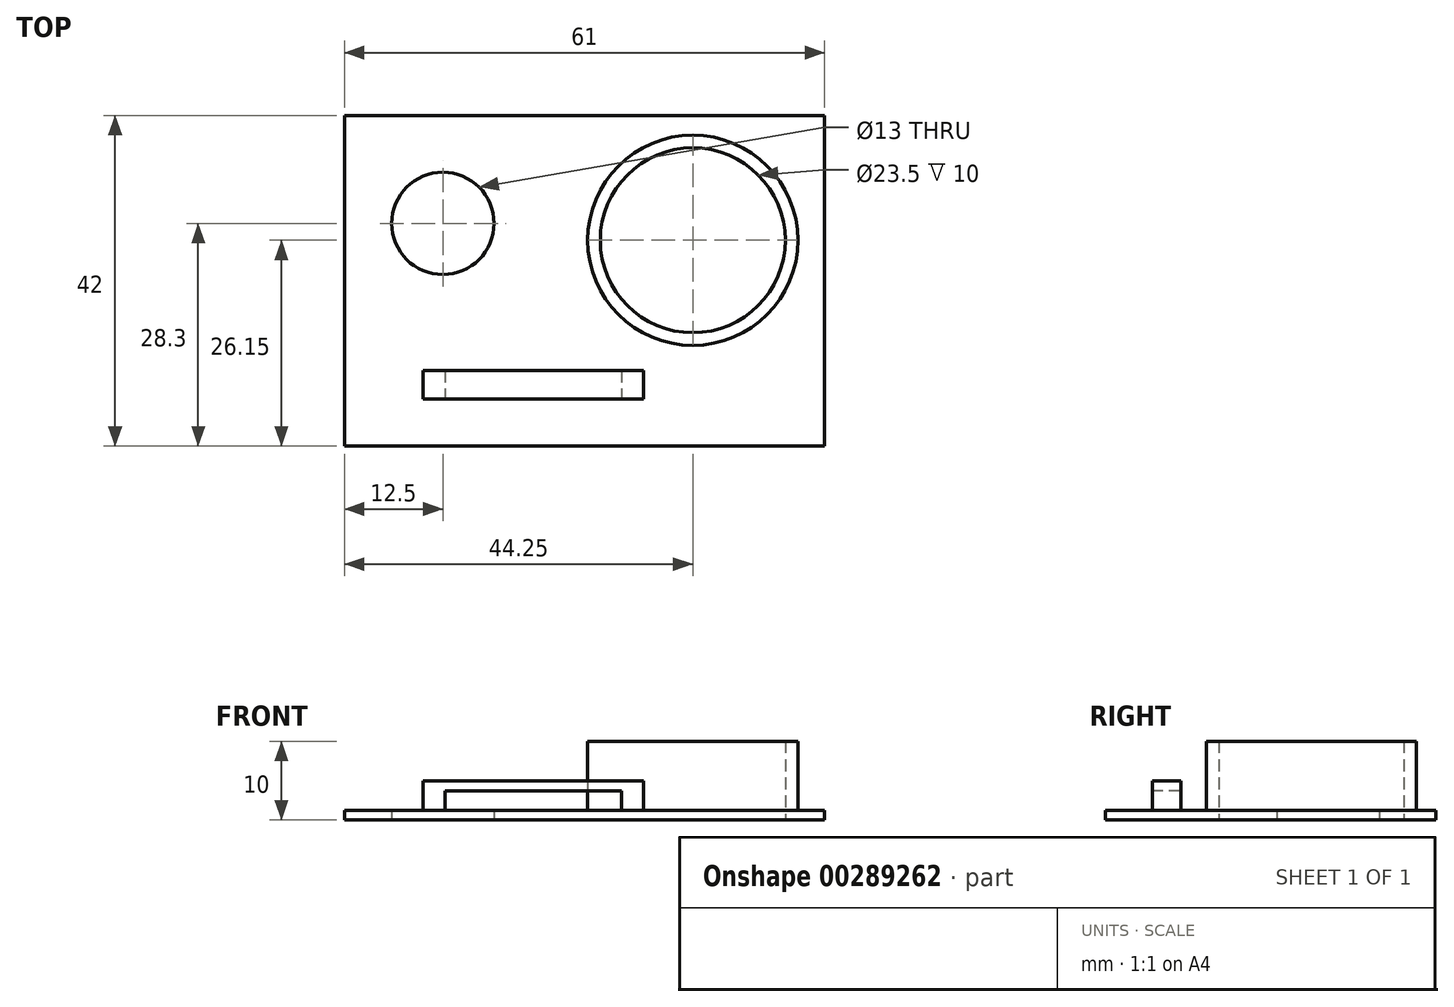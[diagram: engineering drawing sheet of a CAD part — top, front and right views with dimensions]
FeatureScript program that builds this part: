
annotation { "Feature Type Name" : "Feature", "Feature Type Description" : "" }
export const myFeature = defineFeature(function(context is Context, id is Id, definition is map)
    precondition{}
    {
        {
            var Q0;
            Q0=qCreatedBy(makeId("Top.planeOp"),FACE);
            var sketch = newSketch(context, id + "F0", { "sketchPlane" : qUnion([Q0])});
            skLineSegment(sketch, "E0.bottom", {"start": v(0, 0) * mm, "end": v(61, 0) * mm});
            skLineSegment(sketch, "E0.top", {"start": v(0, 42) * mm, "end": v(61, 42) * mm});
            skLineSegment(sketch, "E0.left", {"start": v(0, 0) * mm, "end": v(0, 42) * mm});
            skLineSegment(sketch, "E0.right", {"start": v(61, 0) * mm, "end": v(61, 42) * mm});
            skCircle(sketch, "E1", {"center": v(12.5, 28.3) * mm, "radius": 6.5 * mm});
            skCircle(sketch, "E2", {"center": v(44.25, 26.15) * mm, "radius": 11.75 * mm});
            skCircle(sketch, "E3.0", {"center": v(44.25, 26.15) * mm, "radius": 13.35 * mm});
            skLineSegment(sketch, "E4.bottom", {"start": v(38, 6) * mm, "end": v(10, 6) * mm});
            skLineSegment(sketch, "E4.top", {"start": v(38, 9.6) * mm, "end": v(10, 9.6) * mm});
            skLineSegment(sketch, "E4.left", {"start": v(38, 6) * mm, "end": v(38, 9.6) * mm});
            skLineSegment(sketch, "E4.right", {"start": v(10, 6) * mm, "end": v(10, 9.6) * mm});
            skSolve(sketch);
        }
        {
            var Q0;
            Q0=makeQuery(id+"F0.imprint","IMPRINT",FACE,{"disambiguationData":[TD([[makeQuery(id+"F0.imprint","IMPRINT",EDGE,{"derivedFrom":sQuery(id+"F0.wireOp",EDGE,"E0.bottom")}),1.0]])]});
            var Q1;
            Q1=makeQuery(id+"F0.imprint","IMPRINT",FACE,{"disambiguationData":[TD([[makeQuery(id+"F0.imprint","IMPRINT",EDGE,{"derivedFrom":sQuery(id+"F0.wireOp",EDGE,"E2")}),-1.0]])]});
            extrude(context, id + "F1", {"entities" : qUnion([Q0, Q1]), "depth" : 1.2 * mm});
        }
        {
            var Q0;
            Q0=makeQuery(id+"F0.imprint","IMPRINT",FACE,{"disambiguationData":[TD([[makeQuery(id+"F0.imprint","IMPRINT",EDGE,{"derivedFrom":sQuery(id+"F0.wireOp",EDGE,"E2")}),-1.0]])]});
            extrude(context, id + "F2", {"entities" : qUnion([Q0]), "operationType" : NewBodyOperationType.ADD, "depth" : 10 * mm});
        }
        {
            var Q0;
            Q0=makeQuery(id+"F0.imprint","IMPRINT",FACE,{"disambiguationData":[TD([[makeQuery(id+"F0.imprint","IMPRINT",EDGE,{"derivedFrom":sQuery(id+"F0.wireOp",EDGE,"E4.bottom")}),-1.0]])]});
            extrude(context, id + "F3", {"entities" : qUnion([Q0]), "operationType" : NewBodyOperationType.ADD, "depth" : 5 * mm});
        }
        {
            var Q0;
            Q0=makeQuery(id+"F3.opExtrude","SWEPT_FACE",FACE,{"disambiguationData":[OSD([sQuery(id+"F0.wireOp",EDGE,"E4.bottom")])]});
            var sketch = newSketch(context, id + "F4", { "sketchPlane" : qUnion([Q0])});
            skLineSegment(sketch, "E5.bottom", {"start": v(12.8, 3.7) * mm, "end": v(35.2, 3.7) * mm});
            skLineSegment(sketch, "E5.top", {"start": v(12.8, 1.2) * mm, "end": v(35.2, 1.2) * mm});
            skLineSegment(sketch, "E5.left", {"start": v(12.8, 3.7) * mm, "end": v(12.8, 1.2) * mm});
            skLineSegment(sketch, "E5.right", {"start": v(35.2, 3.7) * mm, "end": v(35.2, 1.2) * mm});
            skSolve(sketch);
        }
        {
            var Q0;
            Q0=makeQuery(id+"F4.imprint","IMPRINT",FACE,{"disambiguationData":[TD([[makeQuery(id+"F4.imprint","IMPRINT",EDGE,{"derivedFrom":sQuery(id+"F4.wireOp",EDGE,"E5.bottom")}),-1.0]])]});
            extrude(context, id + "F5", {"entities" : qUnion([Q0]), "operationType" : NewBodyOperationType.REMOVE, "oppositeDirection" : true, "depth" : 5 * mm});
        }
    });
